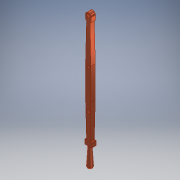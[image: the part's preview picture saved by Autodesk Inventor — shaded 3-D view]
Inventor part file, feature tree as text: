
AUTODESK INVENTOR PART (.ipt)
format: ipt  version: 2017 (Build 210142000, 142)  size: 190,976 bytes
history: native  units: mm
features: sketch x4, extrude x3, plane x1, revolve x1, fillet x1, projected_geometry x1
ambient origin geometry x8: Origin, YZ Plane, XZ Plane, XY Plane, X Axis, Y Axis, Z Axis, Center Point
bodies: Solid1 (feature_tree)
feature tree (11):
  extrude  "Extrusion1"  Depth=3.25mm
  extrude  "Extrusion2"  TaperAngle=0.0deg  [1 undecoded]
  extrude  "Extrusion5"  Depth=3.0mm
  plane  "Work Plane1"
  revolve  "Revolution2"  [1 undecoded]
  fillet  "Fillet1"  Radius=8.0mm
  sketch  "Sketch1"  dims[d0=6.5mm d1=5.0mm d2=6.0mm d3=4.0mm d4=3.5mm d5=90.0deg d6=15.940479mm d7=15.458015mm d8=15.940479mm d9=15.458015mm d10=118.0mm d11=0.25mm d12=6.25mm d13=1.999459mm d14=43.0mm d15=3.25mm d16=78.0mm d17=3.25mm d18=0.0mm d19=3.25mm]
  sketch  "Sketch2"  dims[d20=5.0mm d21=0.0mm]
  sketch  "Sketch6"  dims[d22=2.5mm d23=3.5mm d24=44.0mm d25=3.5mm d26=50.0mm d27=0.0mm d28=0.0mm]
  sketch  "Sketch11"  dims[d43=4.0mm d44=4.0mm d45=5.0mm d46=8.0mm d47=5.0mm d48=0.0mm d66=0.0mm d67=2.0mm d68=3.25mm d72=2.646694mm d73=30.0mm d76=2.646694mm d78=1.5mm d80=30.916343mm d81=6.636616mm d82=0.541052mm d83=90.0deg d84=3.0mm d107=0.489974mm d109=16.962591mm d110=25.3532mm d111=3.065017mm d112=16.962591mm d113=25.3532mm d114=7.146642mm d116=45.0mm d117=0.0mm]
  projected_geometry  "Projected Loop1"
note: 2 required parameter values undecoded (feature->parameter linkage not recoverable at this tier; creation-order binding heuristic only, values carry confidence <= 0.55)